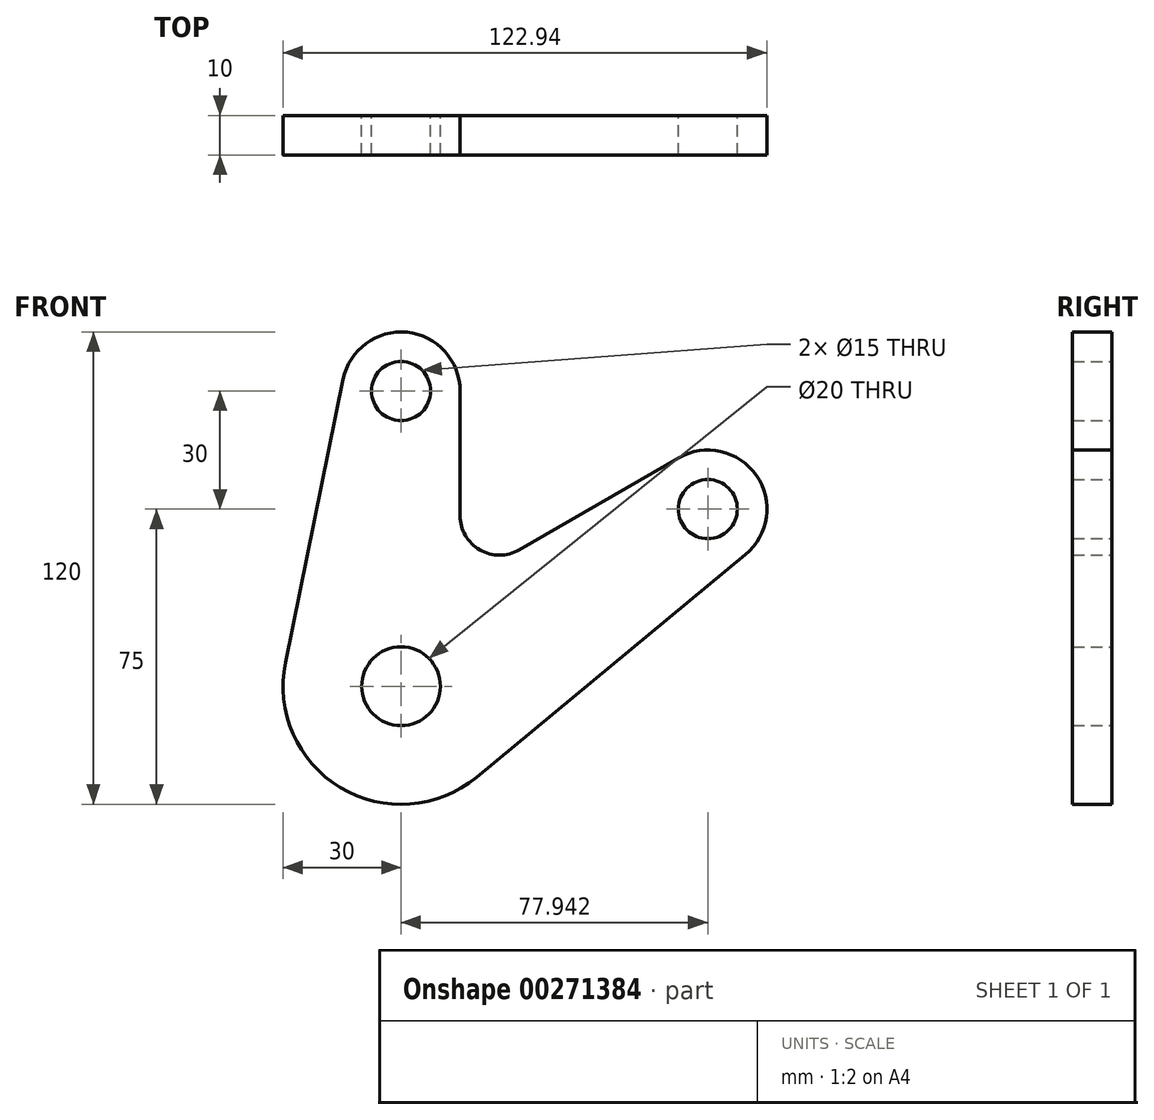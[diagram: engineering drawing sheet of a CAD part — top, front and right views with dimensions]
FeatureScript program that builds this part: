
annotation { "Feature Type Name" : "Feature", "Feature Type Description" : "" }
export const myFeature = defineFeature(function(context is Context, id is Id, definition is map)
    precondition{}
    {
        {
            var Q0;
            Q0=qCreatedBy(makeId("Front.planeOp"),FACE);
            var sketch = newSketch(context, id + "F0", { "sketchPlane" : qUnion([Q0])});
            skCircle(sketch, "E0", {"center": v(0, 0) * mm, "radius": 10 * mm});
            skLineSegment(sketch, "E1", {"start": v(-29.4, 6) * mm, "end": v(-14.7, 78) * mm});
            skArc(sketch, "E2", {"start": v(15, 75) * mm, "mid": v(1.5, 89.92) * mm, "end": v(-14.7, 78) * mm});
            skLineSegment(sketch, "E3", {"start": v(15, 75) * mm, "end": v(15, 43.3) * mm});
            skArc(sketch, "E4", {"start": v(15, 43.3) * mm, "mid": v(20, 34.64) * mm, "end": v(30, 34.64) * mm});
            skLineSegment(sketch, "E5", {"start": v(30, 34.64) * mm, "end": v(70.44, 58) * mm});
            skArc(sketch, "E6", {"start": v(87.5, 33.44) * mm, "mid": v(90.26, 53.56) * mm, "end": v(70.44, 58) * mm});
            skLineSegment(sketch, "E7", {"start": v(87.5, 33.44) * mm, "end": v(19.12, -23.12) * mm});
            skArc(sketch, "E8", {"start": v(-29.4, 6) * mm, "mid": v(-15.44, -25.72) * mm, "end": v(19.12, -23.12) * mm});
            skCircle(sketch, "E9", {"center": v(0, 75) * mm, "radius": 7.5 * mm});
            skCircle(sketch, "E10", {"center": v(77.94, 45) * mm, "radius": 7.5 * mm});
            skLineSegment(sketch, "E11", {"start": v(0, 0) * mm, "end": v(77.94, 45) * mm, "construction": true});
            skLineSegment(sketch, "E12", {"start": v(0, 75) * mm, "end": v(0, 0) * mm, "construction": true});
            skSolve(sketch);
        }
        {
            var Q0;
            Q0 = qSketchRegion(id + "F0", true);
            extrude(context, id + "F1", {"entities" : qUnion([Q0]), "depth" : 10 * mm});
        }
    });
